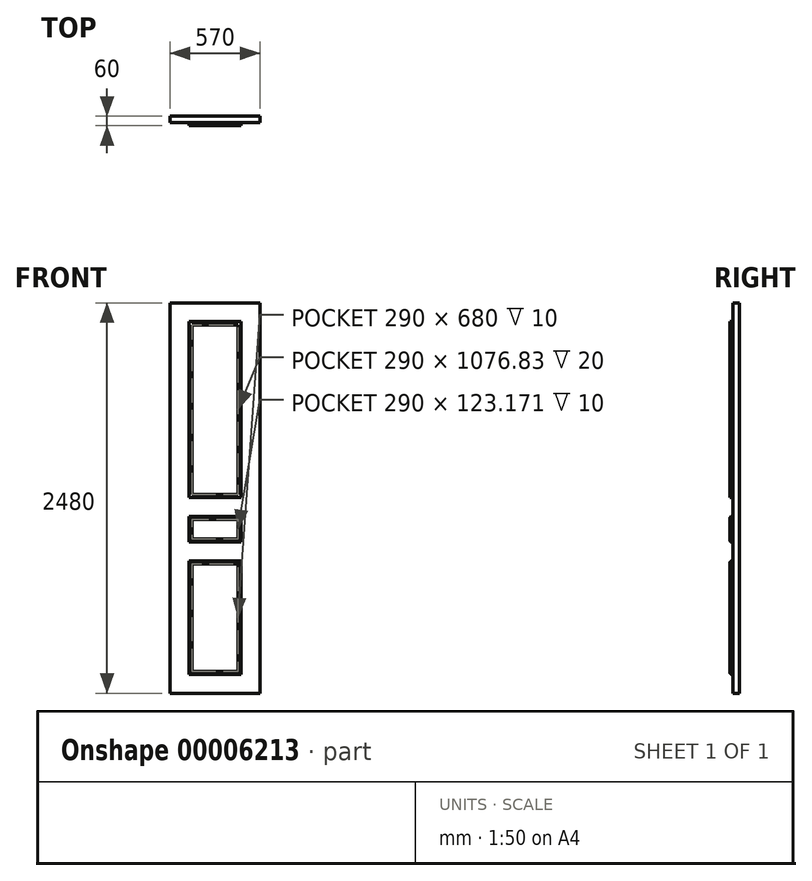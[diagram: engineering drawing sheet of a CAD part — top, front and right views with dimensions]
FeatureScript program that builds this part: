
annotation { "Feature Type Name" : "Feature", "Feature Type Description" : "" }
export const myFeature = defineFeature(function(context is Context, id is Id, definition is map)
    precondition{}
    {
        {
            var Q0;
            Q0=qCreatedBy(makeId("Front.planeOp"),FACE);
            var sketch = newSketch(context, id + "F0", { "sketchPlane" : qUnion([Q0])});
            skLineSegment(sketch, "E0.rect.bottom", {"start": v(285, -1240) * mm, "end": v(-285, -1240) * mm});
            skLineSegment(sketch, "E0.rect.top", {"start": v(285, 1240) * mm, "end": v(-285, 1240) * mm});
            skLineSegment(sketch, "E0.rect.left", {"start": v(285, -1240) * mm, "end": v(285, 1240) * mm});
            skLineSegment(sketch, "E0.rect.right", {"start": v(-285, -1240) * mm, "end": v(-285, 1240) * mm});
            skPoint(sketch, "E0.rect.middle", {"position": v(0, 0) * mm});
            skSolve(sketch);
        }
        {
            var Q0;
            Q0 = qSketchRegion(id + "F0", true);
            extrude(context, id + "F1", {"entities" : qUnion([Q0]), "depth" : 60 * mm});
        }
        {
            var Q0;
            Q0=makeQuery(id+"F1.opExtrude","CAP_FACE",FACE,{"disambiguationData":[OSD([sQuery(id+"F0.wireOp",EDGE,"E0.rect.bottom"),sQuery(id+"F0.wireOp",EDGE,"E0.rect.top"),sQuery(id+"F0.wireOp",EDGE,"E0.rect.left"),sQuery(id+"F0.wireOp",EDGE,"E0.rect.right")])],"isStart":false});
            var sketch = newSketch(context, id + "F2", { "sketchPlane" : qUnion([Q0])});
            skLineSegment(sketch, "E1.rect.bottom", {"start": v(-285, 1240) * mm, "end": v(285, 1240) * mm});
            skLineSegment(sketch, "E1.rect.top", {"start": v(-285, -1240) * mm, "end": v(285, -1240) * mm});
            skLineSegment(sketch, "E1.rect.left", {"start": v(-285, 1240) * mm, "end": v(-285, -1240) * mm});
            skLineSegment(sketch, "E1.rect.right", {"start": v(285, 1240) * mm, "end": v(285, -1240) * mm});
            skPoint(sketch, "E1.rect.middle", {"position": v(0, 0) * mm});
            skLineSegment(sketch, "E2.0", {"start": v(-165, 1120) * mm, "end": v(165, 1120) * mm, "construction": true});
            skLineSegment(sketch, "E2.1", {"start": v(-165, 1120) * mm, "end": v(-165, 3.17) * mm});
            skLineSegment(sketch, "E2.2", {"start": v(-165, -1120) * mm, "end": v(165, -1120) * mm, "construction": true});
            skLineSegment(sketch, "E2.3", {"start": v(165, 1120) * mm, "end": v(165, 3.17) * mm});
            skLineSegment(sketch, "E3.bottom", {"start": v(165, -1120) * mm, "end": v(-165, -1120) * mm});
            skLineSegment(sketch, "E3.top", {"start": v(165, -400) * mm, "end": v(-165, -400) * mm});
            skLineSegment(sketch, "E3.left", {"start": v(165, -1120) * mm, "end": v(165, -400) * mm});
            skLineSegment(sketch, "E3.right", {"start": v(-165, -1120) * mm, "end": v(-165, -400) * mm});
            skLineSegment(sketch, "E4.bottom", {"start": v(-165, -280) * mm, "end": v(165, -280) * mm});
            skLineSegment(sketch, "E4.top", {"start": v(-165, -116.83) * mm, "end": v(165, -116.83) * mm});
            skLineSegment(sketch, "E4.left", {"start": v(-165, -280) * mm, "end": v(-165, -116.83) * mm});
            skLineSegment(sketch, "E4.right", {"start": v(165, -280) * mm, "end": v(165, -116.83) * mm});
            skLineSegment(sketch, "E5.bottom", {"start": v(-165, 1120) * mm, "end": v(165, 1120) * mm});
            skLineSegment(sketch, "E5.top", {"start": v(-165, 3.17) * mm, "end": v(165, 3.17) * mm});
            skLineSegment(sketch, "E6.trimOffspring", {"start": v(165, -116.83) * mm, "end": v(165, -280) * mm});
            skLineSegment(sketch, "E7.trimOffspring", {"start": v(165, -400) * mm, "end": v(165, -1120) * mm});
            skLineSegment(sketch, "E8.trimOffspring", {"start": v(-165, -116.83) * mm, "end": v(-165, -280) * mm});
            skLineSegment(sketch, "E9.trimOffspring", {"start": v(-165, -400) * mm, "end": v(-165, -1120) * mm});
            skLineSegment(sketch, "E10.0", {"start": v(165, 3.17) * mm, "end": v(165, 1120) * mm});
            skLineSegment(sketch, "E10.1", {"start": v(165, 1120) * mm, "end": v(-165, 1120) * mm});
            skLineSegment(sketch, "E10.2", {"start": v(-165, 3.17) * mm, "end": v(-165, 1120) * mm});
            skLineSegment(sketch, "E10.3", {"start": v(165, 3.17) * mm, "end": v(-165, 3.17) * mm});
            skLineSegment(sketch, "E11.0", {"start": v(-145, 1100) * mm, "end": v(145, 1100) * mm});
            skLineSegment(sketch, "E11.1", {"start": v(-145, 1100) * mm, "end": v(-145, 23.17) * mm});
            skLineSegment(sketch, "E11.2", {"start": v(-145, 23.17) * mm, "end": v(145, 23.17) * mm});
            skLineSegment(sketch, "E11.3", {"start": v(145, 1100) * mm, "end": v(145, 23.17) * mm});
            skLineSegment(sketch, "E12.0", {"start": v(-145, -136.83) * mm, "end": v(145, -136.83) * mm});
            skLineSegment(sketch, "E12.1", {"start": v(-145, -136.83) * mm, "end": v(-145, -260) * mm});
            skLineSegment(sketch, "E12.2", {"start": v(-145, -260) * mm, "end": v(145, -260) * mm});
            skLineSegment(sketch, "E12.3", {"start": v(145, -260) * mm, "end": v(145, -136.83) * mm});
            skLineSegment(sketch, "E13.0", {"start": v(145, -420) * mm, "end": v(-145, -420) * mm});
            skLineSegment(sketch, "E13.1", {"start": v(145, -420) * mm, "end": v(145, -1100) * mm});
            skLineSegment(sketch, "E13.2", {"start": v(-145, -1100) * mm, "end": v(145, -1100) * mm});
            skLineSegment(sketch, "E13.3", {"start": v(-145, -1100) * mm, "end": v(-145, -420) * mm});
            skSolve(sketch);
        }
        {
            var Q0;
            Q0=makeQuery(id+"F2.imprint","IMPRINT",FACE,{"disambiguationData":[TD([[makeQuery(id+"F2.imprint","IMPRINT",EDGE,{"derivedFrom":sQuery(id+"F2.wireOp",EDGE,"E11.0")}),-1.0]])]});
            var Q1;
            Q1=makeQuery(id+"F2.imprint","IMPRINT",FACE,{"disambiguationData":[TD([[makeQuery(id+"F2.imprint","IMPRINT",EDGE,{"derivedFrom":sQuery(id+"F2.wireOp",EDGE,"E1.rect.bottom")}),1.0]])]});
            var Q2;
            Q2=makeQuery(id+"F2.imprint","IMPRINT",FACE,{"disambiguationData":[TD([[makeQuery(id+"F2.imprint","IMPRINT",EDGE,{"derivedFrom":sQuery(id+"F2.wireOp",EDGE,"E13.0")}),1.0]])]});
            var Q3;
            Q3=makeQuery(id+"F2.imprint","IMPRINT",FACE,{"disambiguationData":[TD([[makeQuery(id+"F2.imprint","IMPRINT",EDGE,{"derivedFrom":sQuery(id+"F2.wireOp",EDGE,"E12.0")}),-1.0]])]});
            extrude(context, id + "F3", {"entities" : qUnion([Q0, Q1, Q2, Q3]), "operationType" : NewBodyOperationType.REMOVE, "oppositeDirection" : true, "depth" : 20 * mm});
        }
        {
            var Q0;
            Q0=makeQuery(id+"F3.boolean.opBoolean","SPLIT",FACE,{"disambiguationData":[TD([makeQuery(id+"F3.opExtrude","SWEPT_FACE",FACE,{"disambiguationData":[OSD([sQuery(id+"F2.wireOp",EDGE,"E10.0")])]})])],"derivedFrom":makeQuery(id+"F1.opExtrude","CAP_FACE",FACE,{"disambiguationData":[OSD([sQuery(id+"F0.wireOp",EDGE,"E0.rect.bottom"),sQuery(id+"F0.wireOp",EDGE,"E0.rect.top"),sQuery(id+"F0.wireOp",EDGE,"E0.rect.left"),sQuery(id+"F0.wireOp",EDGE,"E0.rect.right")])],"isStart":false})});
            var Q1;
            Q1=makeQuery(id+"F3.boolean.opBoolean","SPLIT",FACE,{"disambiguationData":[TD([makeQuery(id+"F3.opExtrude","SWEPT_FACE",FACE,{"disambiguationData":[OSD([sQuery(id+"F2.wireOp",EDGE,"E4.bottom")])]})])],"derivedFrom":makeQuery(id+"F1.opExtrude","CAP_FACE",FACE,{"disambiguationData":[OSD([sQuery(id+"F0.wireOp",EDGE,"E0.rect.bottom"),sQuery(id+"F0.wireOp",EDGE,"E0.rect.top"),sQuery(id+"F0.wireOp",EDGE,"E0.rect.left"),sQuery(id+"F0.wireOp",EDGE,"E0.rect.right")])],"isStart":false})});
            var Q2;
            Q2=makeQuery(id+"F3.boolean.opBoolean","SPLIT",FACE,{"disambiguationData":[TD([makeQuery(id+"F3.opExtrude","SWEPT_FACE",FACE,{"disambiguationData":[OSD([sQuery(id+"F2.wireOp",EDGE,"E3.bottom")])]})])],"derivedFrom":makeQuery(id+"F1.opExtrude","CAP_FACE",FACE,{"disambiguationData":[OSD([sQuery(id+"F0.wireOp",EDGE,"E0.rect.bottom"),sQuery(id+"F0.wireOp",EDGE,"E0.rect.top"),sQuery(id+"F0.wireOp",EDGE,"E0.rect.left"),sQuery(id+"F0.wireOp",EDGE,"E0.rect.right")])],"isStart":false})});
            fillet(context, id + "F4", {"entities" : qUnion([Q0, Q1, Q2]), "radius" : 10 * mm, "tangentPropagation" : true, "allowEdgeOverflow" : false});
        }
    });
